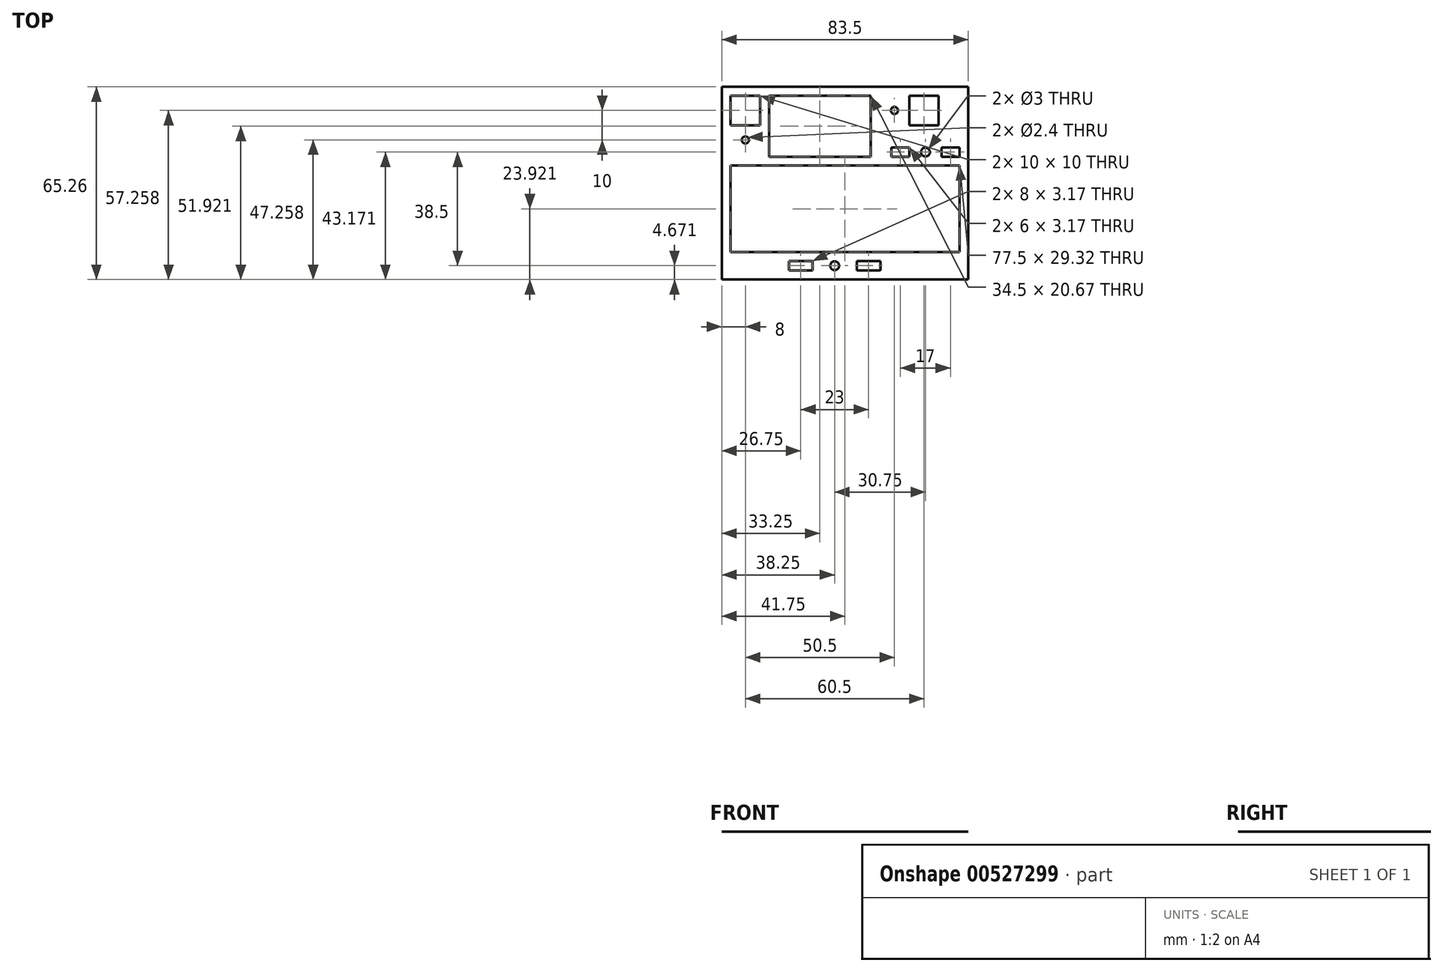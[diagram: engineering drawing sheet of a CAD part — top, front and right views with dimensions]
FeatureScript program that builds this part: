
annotation { "Feature Type Name" : "Feature", "Feature Type Description" : "" }
export const myFeature = defineFeature(function(context is Context, id is Id, definition is map)
    precondition{}
    {
        {
            var Q0;
            Q0=qCreatedBy(makeId("Top.planeOp"),FACE);
            var sketch = newSketch(context, id + "F0", { "sketchPlane" : qUnion([Q0])});
            skLineSegment(sketch, "E0.bottom", {"start": v(-47.72, 57.4) * mm, "end": v(35.78, 57.4) * mm});
            skLineSegment(sketch, "E0.top", {"start": v(-47.72, -7.85) * mm, "end": v(35.78, -7.85) * mm});
            skLineSegment(sketch, "E0.left", {"start": v(-47.72, 57.4) * mm, "end": v(-47.72, -7.85) * mm});
            skLineSegment(sketch, "E0.right", {"start": v(35.78, 57.4) * mm, "end": v(35.78, -7.85) * mm});
            skCircle(sketch, "E1", {"center": v(-9.47, -3.18) * mm, "radius": 1.5 * mm});
            skLineSegment(sketch, "E2.bottom", {"start": v(-1.97, -1.6) * mm, "end": v(6.03, -1.6) * mm});
            skLineSegment(sketch, "E2.top", {"start": v(-1.97, -4.77) * mm, "end": v(6.03, -4.77) * mm});
            skLineSegment(sketch, "E2.left", {"start": v(-1.97, -1.6) * mm, "end": v(-1.97, -4.77) * mm});
            skLineSegment(sketch, "E2.right", {"start": v(6.03, -1.6) * mm, "end": v(6.03, -4.77) * mm});
            skPoint(sketch, "E2.middle", {"position": v(2.03, -3.18) * mm});
            skLineSegment(sketch, "E3", {"start": v(-9.47, -3.18) * mm, "end": v(-9.47, -4.68) * mm});
            skLineSegment(sketch, "E4.MirrorCS", {"start": v(-16.97, -1.6) * mm, "end": v(-16.97, -4.77) * mm});
            skLineSegment(sketch, "E5.MirrorCS", {"start": v(-16.97, -1.6) * mm, "end": v(-24.97, -1.6) * mm});
            skLineSegment(sketch, "E6.MirrorCS", {"start": v(-24.97, -1.6) * mm, "end": v(-24.97, -4.77) * mm});
            skLineSegment(sketch, "E7.MirrorCS", {"start": v(-16.97, -4.77) * mm, "end": v(-24.97, -4.77) * mm});
            skLineSegment(sketch, "E8.bottom", {"start": v(-44.72, 44.4) * mm, "end": v(-34.72, 44.4) * mm});
            skLineSegment(sketch, "E8.top", {"start": v(-44.72, 34.4) * mm, "end": v(-34.72, 34.4) * mm});
            skLineSegment(sketch, "E8.left", {"start": v(-44.72, 44.4) * mm, "end": v(-44.72, 34.4) * mm});
            skLineSegment(sketch, "E8.right", {"start": v(-34.72, 44.4) * mm, "end": v(-34.72, 34.4) * mm});
            skPoint(sketch, "E8.middle", {"position": v(-39.72, 39.4) * mm});
            skLineSegment(sketch, "E9.top", {"start": v(-44.72, 54.4) * mm, "end": v(-34.72, 54.4) * mm});
            skLineSegment(sketch, "E9.left", {"start": v(-44.72, 44.4) * mm, "end": v(-44.72, 54.4) * mm});
            skLineSegment(sketch, "E9.right", {"start": v(-34.72, 44.4) * mm, "end": v(-34.72, 54.4) * mm});
            skCircle(sketch, "E10", {"center": v(-39.72, 39.4) * mm, "radius": 1.2 * mm});
            skLineSegment(sketch, "E11.bottom", {"start": v(15.78, 44.4) * mm, "end": v(25.78, 44.4) * mm});
            skLineSegment(sketch, "E12.top", {"start": v(15.78, 54.4) * mm, "end": v(25.78, 54.4) * mm});
            skLineSegment(sketch, "E12.left", {"start": v(15.78, 44.4) * mm, "end": v(15.78, 54.4) * mm});
            skLineSegment(sketch, "E12.right", {"start": v(25.78, 44.4) * mm, "end": v(25.78, 54.4) * mm});
            skLineSegment(sketch, "E13.bottom", {"start": v(15.78, 54.4) * mm, "end": v(5.78, 54.4) * mm});
            skLineSegment(sketch, "E13.top", {"start": v(15.78, 44.4) * mm, "end": v(5.78, 44.4) * mm});
            skLineSegment(sketch, "E13.left", {"start": v(15.78, 54.4) * mm, "end": v(15.78, 44.4) * mm});
            skLineSegment(sketch, "E13.right", {"start": v(5.78, 54.4) * mm, "end": v(5.78, 44.4) * mm});
            skCircle(sketch, "E14", {"center": v(10.78, 49.4) * mm, "radius": 1.2 * mm});
            skPoint(sketch, "E14.centerSnap0", {"position": v(15.78, 49.4) * mm});
            skCircle(sketch, "E15", {"center": v(21.28, 35.32) * mm, "radius": 1.5 * mm});
            skLineSegment(sketch, "E16.bottom", {"start": v(26.78, 36.9) * mm, "end": v(32.78, 36.9) * mm});
            skLineSegment(sketch, "E16.top", {"start": v(26.78, 33.73) * mm, "end": v(32.78, 33.73) * mm});
            skLineSegment(sketch, "E16.left", {"start": v(26.78, 36.9) * mm, "end": v(26.78, 33.73) * mm});
            skLineSegment(sketch, "E16.right", {"start": v(32.78, 36.9) * mm, "end": v(32.78, 33.73) * mm});
            skPoint(sketch, "E16.middle", {"position": v(29.78, 35.32) * mm});
            skLineSegment(sketch, "E17", {"start": v(21.28, 35.32) * mm, "end": v(21.28, 33.82) * mm});
            skLineSegment(sketch, "E18.MirrorCS", {"start": v(15.78, 36.9) * mm, "end": v(15.78, 33.73) * mm});
            skLineSegment(sketch, "E19.MirrorCS", {"start": v(15.78, 36.9) * mm, "end": v(9.78, 36.9) * mm});
            skLineSegment(sketch, "E20.MirrorCS", {"start": v(9.78, 36.9) * mm, "end": v(9.78, 33.73) * mm});
            skLineSegment(sketch, "E21.MirrorCS", {"start": v(15.78, 33.73) * mm, "end": v(9.78, 33.73) * mm});
            skLineSegment(sketch, "E22.bottom", {"start": v(-44.72, 1.4) * mm, "end": v(32.78, 1.4) * mm});
            skLineSegment(sketch, "E22.top", {"start": v(-44.72, 30.73) * mm, "end": v(32.78, 30.73) * mm});
            skLineSegment(sketch, "E22.left", {"start": v(-44.72, 1.4) * mm, "end": v(-44.72, 30.73) * mm});
            skLineSegment(sketch, "E22.right", {"start": v(32.78, 1.4) * mm, "end": v(32.78, 30.73) * mm});
            skLineSegment(sketch, "E23.bottom", {"start": v(-31.72, 54.4) * mm, "end": v(2.78, 54.4) * mm});
            skLineSegment(sketch, "E23.top", {"start": v(-31.72, 33.73) * mm, "end": v(2.78, 33.73) * mm});
            skLineSegment(sketch, "E23.left", {"start": v(-31.72, 54.4) * mm, "end": v(-31.72, 33.73) * mm});
            skLineSegment(sketch, "E23.right", {"start": v(2.78, 54.4) * mm, "end": v(2.78, 33.73) * mm});
            skSolve(sketch);
        }
        {
            var Q0;
            {var subQ3=sQuery(id+"F0.wireOp",EDGE,"HT0FgSfA-p8Ka-Uasf-GnQQ-7LQ1lVp28IHL.bottom");Q0=makeQuery(id+"F0.imprint","IMPRINT",FACE,{"disambiguationData":[TD([[makeQuery(id+"F0.imprint","IMPRINT",EDGE,{"derivedFrom":subQ3}),1.0]])]});}
            var Q1;
            Q1=makeQuery(id+"F0.imprint","IMPRINT",FACE,{"disambiguationData":[TD([[makeQuery(id+"F0.imprint","IMPRINT",EDGE,{"derivedFrom":sQuery(id+"F0.wireOp",EDGE,"E8.top")}),1.0]])]});
            var Q2;
            Q2=makeQuery(id+"F0.imprint","IMPRINT",FACE,{"disambiguationData":[TD([[makeQuery(id+"F0.imprint","IMPRINT",EDGE,{"derivedFrom":sQuery(id+"F0.wireOp",EDGE,"E11.top")}),1.0]])]});
            var Q3;
            Q3=makeQuery(id+"F0.imprint","IMPRINT",FACE,{"disambiguationData":[TD([[makeQuery(id+"F0.imprint","IMPRINT",EDGE,{"derivedFrom":sQuery(id+"F0.wireOp",EDGE,"E0.bottom")}),-1.0]])]});
            var Q4;
            Q4=makeQuery(id+"F0.imprint","IMPRINT",FACE,{"disambiguationData":[TD([[makeQuery(id+"F0.imprint","IMPRINT",EDGE,{"derivedFrom":sQuery(id+"F0.wireOp",EDGE,"E13.bottom")}),1.0]])]});
            var Q5;
            {var subQ1=sQuery(id+"F0.wireOp",EDGE,"E22.top");var subQ3=sQuery(id+"F0.wireOp",EDGE,"lJPrniQo-KQlQ-myDD-NT2K-7scDdSdOlcIJ");var subQ4=makeQuery(id+"F0.imprint","INTERSECT",VERTEX,{"derivedFrom":[subQ1,subQ3]});Q5=makeQuery(id+"F0.imprint","IMPRINT",FACE,{"disambiguationData":[TD([[makeQuery(id+"F0.imprint","IMPRINT",EDGE,{"disambiguationData":[TD([[subQ4,-1.0]])],"derivedFrom":subQ3}),-1.0]])]});}
            var Q6;
            {var subQ1=sQuery(id+"F0.wireOp",EDGE,"E22.left");var subQ3=sQuery(id+"F0.wireOp",EDGE,"clPjOm5P-kCzo-kHEJ-Mq46-RzS6wSXf1xcr");var subQ4=makeQuery(id+"F0.imprint","INTERSECT",VERTEX,{"derivedFrom":[subQ1,subQ3]});Q6=makeQuery(id+"F0.imprint","IMPRINT",FACE,{"disambiguationData":[TD([[makeQuery(id+"F0.imprint","IMPRINT",EDGE,{"disambiguationData":[TD([[subQ4,-1.0]])],"derivedFrom":subQ3}),1.0]])]});}
            var Q7;
            {var subQ0=sQuery(id+"F0.wireOp",EDGE,"zX3S5Jjs-xloe-I1Ss-XtsY-LCYhuaSpaZwi");var subQ5=sQuery(id+"F0.wireOp",EDGE,"clPjOm5P-kCzo-kHEJ-Mq46-RzS6wSXf1xcr");var subQ6=makeQuery(id+"F0.imprint","INTERSECT",VERTEX,{"derivedFrom":[subQ0,subQ5]});Q7=makeQuery(id+"F0.imprint","IMPRINT",FACE,{"disambiguationData":[TD([[makeQuery(id+"F0.imprint","IMPRINT",EDGE,{"disambiguationData":[TD([[subQ6,1.0]])],"derivedFrom":subQ5}),-1.0]])]});}
            var Q8;
            {var subQ0=sQuery(id+"F0.wireOp",EDGE,"zX3S5Jjs-xloe-I1Ss-XtsY-LCYhuaSpaZwi");var subQ5=sQuery(id+"F0.wireOp",EDGE,"clPjOm5P-kCzo-kHEJ-Mq46-RzS6wSXf1xcr");var subQ6=makeQuery(id+"F0.imprint","INTERSECT",VERTEX,{"derivedFrom":[subQ0,subQ5]});Q8=makeQuery(id+"F0.imprint","IMPRINT",FACE,{"disambiguationData":[TD([[makeQuery(id+"F0.imprint","IMPRINT",EDGE,{"disambiguationData":[TD([[subQ6,-1.0]])],"derivedFrom":subQ5}),-1.0]])]});}
            var Q9;
            {var subQ1=sQuery(id+"F0.wireOp",EDGE,"E22.bottom");var subQ3=sQuery(id+"F0.wireOp",EDGE,"clPjOm5P-kCzo-kHEJ-Mq46-RzS6wSXf1xcr");var subQ4=makeQuery(id+"F0.imprint","INTERSECT",VERTEX,{"derivedFrom":[subQ1,subQ3]});Q9=makeQuery(id+"F0.imprint","IMPRINT",FACE,{"disambiguationData":[TD([[makeQuery(id+"F0.imprint","IMPRINT",EDGE,{"disambiguationData":[TD([[subQ4,1.0]])],"derivedFrom":subQ3}),1.0]])]});}
            var Q10;
            {var subQ1=sQuery(id+"F0.wireOp",EDGE,"E22.right");var subQ3=sQuery(id+"F0.wireOp",EDGE,"lJPrniQo-KQlQ-myDD-NT2K-7scDdSdOlcIJ");var subQ4=makeQuery(id+"F0.imprint","INTERSECT",VERTEX,{"derivedFrom":[subQ1,subQ3]});Q10=makeQuery(id+"F0.imprint","IMPRINT",FACE,{"disambiguationData":[TD([[makeQuery(id+"F0.imprint","IMPRINT",EDGE,{"disambiguationData":[TD([[subQ4,1.0]])],"derivedFrom":subQ3}),-1.0]])]});}
            var Q11;
            {var subQ0=sQuery(id+"F0.wireOp",EDGE,"zX3S5Jjs-xloe-I1Ss-XtsY-LCYhuaSpaZwi");var subQ5=sQuery(id+"F0.wireOp",EDGE,"lJPrniQo-KQlQ-myDD-NT2K-7scDdSdOlcIJ");var subQ6=makeQuery(id+"F0.imprint","INTERSECT",VERTEX,{"derivedFrom":[subQ0,subQ5]});Q11=makeQuery(id+"F0.imprint","IMPRINT",FACE,{"disambiguationData":[TD([[makeQuery(id+"F0.imprint","IMPRINT",EDGE,{"disambiguationData":[TD([[subQ6,-1.0]])],"derivedFrom":subQ5}),1.0]])]});}
            var Q12;
            {var subQ0=sQuery(id+"F0.wireOp",EDGE,"zX3S5Jjs-xloe-I1Ss-XtsY-LCYhuaSpaZwi");var subQ5=sQuery(id+"F0.wireOp",EDGE,"lJPrniQo-KQlQ-myDD-NT2K-7scDdSdOlcIJ");var subQ6=makeQuery(id+"F0.imprint","INTERSECT",VERTEX,{"derivedFrom":[subQ0,subQ5]});Q12=makeQuery(id+"F0.imprint","IMPRINT",FACE,{"disambiguationData":[TD([[makeQuery(id+"F0.imprint","IMPRINT",EDGE,{"disambiguationData":[TD([[subQ6,1.0]])],"derivedFrom":subQ5}),1.0]])]});}
            var Q13;
            {var subQ0=sQuery(id+"F0.wireOp",EDGE,"wNFUc8b0-gjkI-0nbu-oo1O-OLY514yP2wiv");var subQ1=sQuery(id+"F0.wireOp",EDGE,"3Xf6nMQ7-GNYa-lfuw-9W0w-KMg57BGVG2Uk");var subQ2=makeQuery(id+"F0.imprint","INTERSECT",VERTEX,{"derivedFrom":[subQ1,subQ0]});Q13=makeQuery(id+"F0.imprint","IMPRINT",FACE,{"disambiguationData":[TD([[makeQuery(id+"F0.imprint","IMPRINT",EDGE,{"disambiguationData":[TD([[subQ2,-1.0]])],"derivedFrom":subQ1}),1.0]])]});}
            var Q14;
            {var subQ0=sQuery(id+"F0.wireOp",EDGE,"zX3S5Jjs-xloe-I1Ss-XtsY-LCYhuaSpaZwi");var subQ1=sQuery(id+"F0.wireOp",EDGE,"3Xf6nMQ7-GNYa-lfuw-9W0w-KMg57BGVG2Uk");var subQ2=makeQuery(id+"F0.imprint","INTERSECT",VERTEX,{"derivedFrom":[subQ1,subQ0]});Q14=makeQuery(id+"F0.imprint","IMPRINT",FACE,{"disambiguationData":[TD([[makeQuery(id+"F0.imprint","IMPRINT",EDGE,{"disambiguationData":[TD([[subQ2,-1.0]])],"derivedFrom":subQ1}),1.0]])]});}
            var Q15;
            {var subQ0=sQuery(id+"F0.wireOp",EDGE,"wNFUc8b0-gjkI-0nbu-oo1O-OLY514yP2wiv");var subQ1=sQuery(id+"F0.wireOp",EDGE,"3Xf6nMQ7-GNYa-lfuw-9W0w-KMg57BGVG2Uk");var subQ2=makeQuery(id+"F0.imprint","INTERSECT",VERTEX,{"derivedFrom":[subQ1,subQ0]});Q15=makeQuery(id+"F0.imprint","IMPRINT",FACE,{"disambiguationData":[TD([[makeQuery(id+"F0.imprint","IMPRINT",EDGE,{"disambiguationData":[TD([[subQ2,-1.0]])],"derivedFrom":subQ1}),-1.0]])]});}
            var Q16;
            {var subQ0=sQuery(id+"F0.wireOp",EDGE,"zX3S5Jjs-xloe-I1Ss-XtsY-LCYhuaSpaZwi");var subQ1=sQuery(id+"F0.wireOp",EDGE,"3Xf6nMQ7-GNYa-lfuw-9W0w-KMg57BGVG2Uk");var subQ2=makeQuery(id+"F0.imprint","INTERSECT",VERTEX,{"derivedFrom":[subQ1,subQ0]});Q16=makeQuery(id+"F0.imprint","IMPRINT",FACE,{"disambiguationData":[TD([[makeQuery(id+"F0.imprint","IMPRINT",EDGE,{"disambiguationData":[TD([[subQ2,-1.0]])],"derivedFrom":subQ1}),-1.0]])]});}
            extrude(context, id + "F1", {"entities" : qUnion([Q0, Q1, Q2, Q3, Q4, Q5, Q6, Q7, Q8, Q9, Q10, Q11, Q12, Q13, Q14, Q15, Q16]), "depth" : 1 / 203.2 * mm, "offsetDistance" : 25 * mm});
        }
    });
